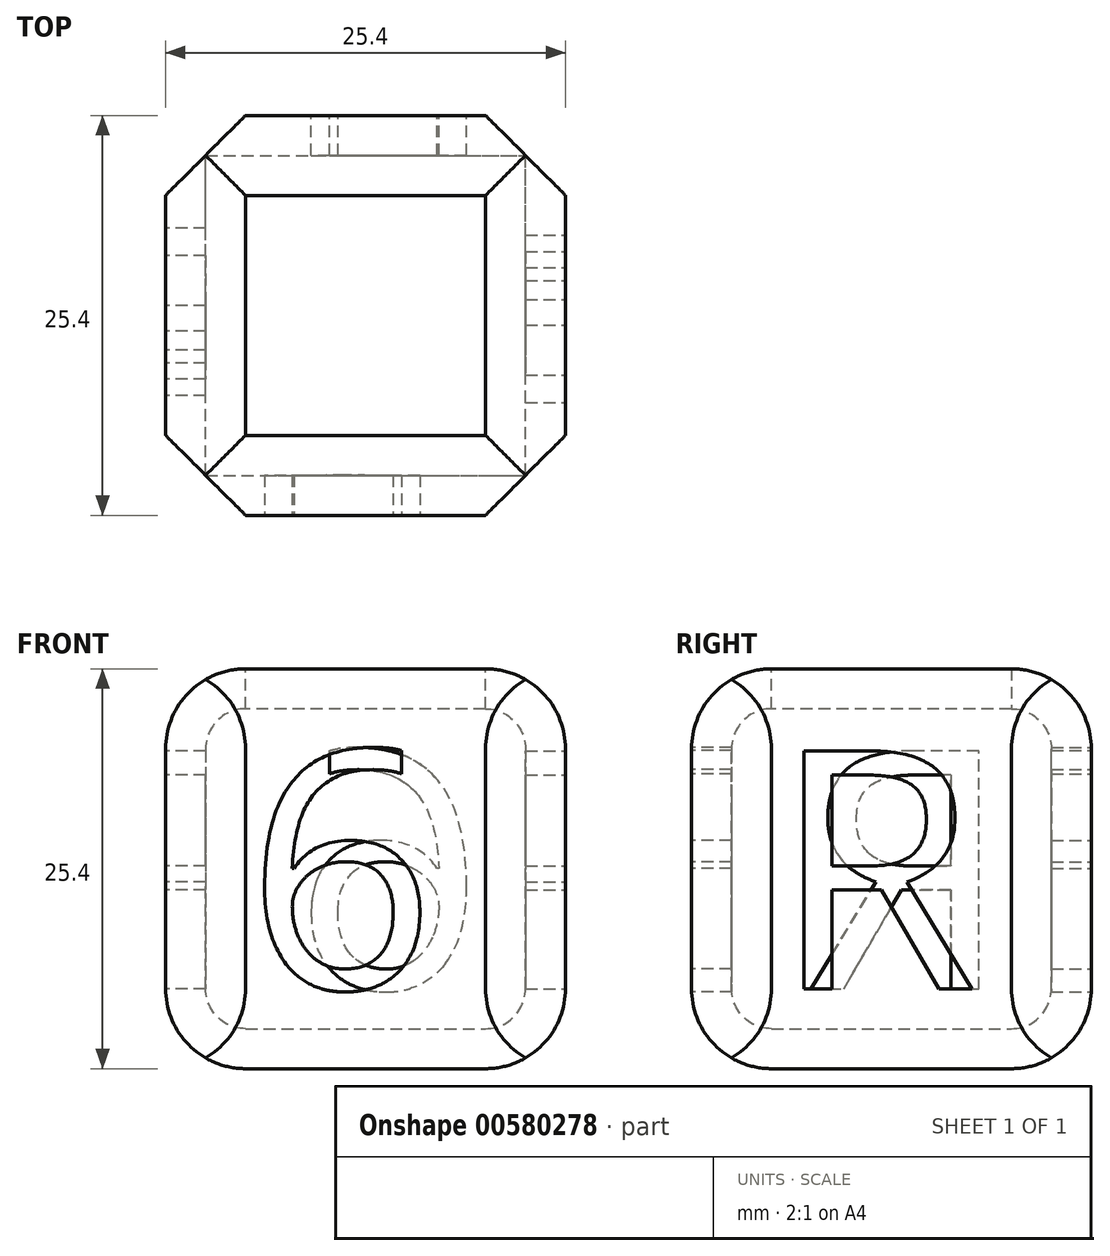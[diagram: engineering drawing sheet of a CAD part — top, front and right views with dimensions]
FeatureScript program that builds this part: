
annotation { "Feature Type Name" : "Feature", "Feature Type Description" : "" }
export const myFeature = defineFeature(function(context is Context, id is Id, definition is map)
    precondition{}
    {
        {
            var Q0;
            Q0=qCreatedBy(makeId("Front.planeOp"),FACE);
            var sketch = newSketch(context, id + "F0", { "sketchPlane" : qUnion([Q0])});
            skLineSegment(sketch, "E0.bottom", {"start": v(-12.7, 12.7) * mm, "end": v(12.7, 12.7) * mm});
            skLineSegment(sketch, "E0.top", {"start": v(-12.7, -12.7) * mm, "end": v(12.7, -12.7) * mm});
            skLineSegment(sketch, "E0.left", {"start": v(-12.7, 12.7) * mm, "end": v(-12.7, -12.7) * mm});
            skLineSegment(sketch, "E0.right", {"start": v(12.7, 12.7) * mm, "end": v(12.7, -12.7) * mm});
            skPoint(sketch, "E0.middle", {"position": v(0, 0) * mm});
            skSolve(sketch);
        }
        {
            var Q0;
            Q0=makeQuery(id+"F0.imprint","IMPRINT",FACE,{"disambiguationData":[TD([[makeQuery(id+"F0.imprint","IMPRINT",EDGE,{"derivedFrom":sQuery(id+"F0.wireOp",EDGE,"E0.bottom")}),-1.0]])]});
            extrude(context, id + "F1", {"entities" : qUnion([Q0]), "depth" : 25.4 * mm, "offsetDistance" : 25.4 * mm});
        }
        {
            var Q0;
            Q0=makeQuery(id+"F1.opExtrude","SWEPT_FACE",FACE,{"disambiguationData":[OSD([sQuery(id+"F0.wireOp",EDGE,"E0.bottom")])]});
            var Q1;
            Q1=makeQuery(id+"F1.opExtrude","SWEPT_FACE",FACE,{"disambiguationData":[OSD([sQuery(id+"F0.wireOp",EDGE,"E0.top")])]});
            fillet(context, id + "F2", {"entities" : qUnion([Q0, Q1]), "radius" : 5.08 * mm, "tangentPropagation" : true, "allowEdgeOverflow" : false});
        }
        {
            var Q0;
            Q0=makeQuery(id+"F1.opExtrude","CAP_FACE",FACE,{"disambiguationData":[OSD([sQuery(id+"F0.wireOp",EDGE,"E0.bottom"),sQuery(id+"F0.wireOp",EDGE,"E0.top"),sQuery(id+"F0.wireOp",EDGE,"E0.left"),sQuery(id+"F0.wireOp",EDGE,"E0.right")])],"isStart":false});
            var Q1;
            Q1=makeQuery(id+"F1.opExtrude","SWEPT_FACE",FACE,{"disambiguationData":[OSD([sQuery(id+"F0.wireOp",EDGE,"E0.right")])]});
            var Q2;
            Q2=makeQuery(id+"F1.opExtrude","CAP_FACE",FACE,{"disambiguationData":[OSD([sQuery(id+"F0.wireOp",EDGE,"E0.bottom"),sQuery(id+"F0.wireOp",EDGE,"E0.top"),sQuery(id+"F0.wireOp",EDGE,"E0.left"),sQuery(id+"F0.wireOp",EDGE,"E0.right")])],"isStart":true});
            var Q3;
            Q3=makeQuery(id+"F1.opExtrude","SWEPT_FACE",FACE,{"disambiguationData":[OSD([sQuery(id+"F0.wireOp",EDGE,"E0.left")])]});
            chamfer(context, id + "F3", {"entities" : qUnion([Q0, Q1, Q2, Q3]), "width" : 5.08 * mm, "tangentPropagation" : true});
        }
        {
            var Q0;
            {var subQ0=sQuery(id+"F0.wireOp",EDGE,"E0.left");Q0=makeQuery(id+"F3.opChamfer","BLEND_FACE",FACE,{"disambiguationData":[OSD([subQ0]),TDD([makeQuery(id+"F1.opExtrude","CAP_EDGE",EDGE,{"disambiguationData":[OSD([subQ0])],"isStart":false})])]});}
            var Q1;
            {var subQ0=sQuery(id+"F0.wireOp",EDGE,"E0.left");Q1=makeQuery(id+"F3.opChamfer","BLEND_FACE",FACE,{"disambiguationData":[OSD([subQ0]),TDD([makeQuery(id+"F1.opExtrude","CAP_EDGE",EDGE,{"disambiguationData":[OSD([subQ0])],"isStart":true})])]});}
            var Q2;
            {var subQ0=sQuery(id+"F0.wireOp",EDGE,"E0.right");Q2=makeQuery(id+"F3.opChamfer","BLEND_FACE",FACE,{"disambiguationData":[OSD([subQ0]),TDD([makeQuery(id+"F1.opExtrude","CAP_EDGE",EDGE,{"disambiguationData":[OSD([subQ0])],"isStart":true})])]});}
            var Q3;
            {var subQ0=sQuery(id+"F0.wireOp",EDGE,"E0.right");Q3=makeQuery(id+"F3.opChamfer","BLEND_FACE",FACE,{"disambiguationData":[OSD([subQ0]),TDD([makeQuery(id+"F1.opExtrude","CAP_EDGE",EDGE,{"disambiguationData":[OSD([subQ0])],"isStart":false})])]});}
            var Q4;
            Q4=makeQuery(id+"F1.opExtrude","SWEPT_FACE",FACE,{"disambiguationData":[OSD([sQuery(id+"F0.wireOp",EDGE,"E0.bottom")])]});
            shell(context, id + "F4", {"entities" : qUnion([Q0, Q1, Q2, Q3, Q4]), "thickness" : 2.54 * mm});
        }
        {
            var Q0;
            Q0=makeQuery(id+"F1.opExtrude","CAP_FACE",FACE,{"disambiguationData":[OSD([sQuery(id+"F0.wireOp",EDGE,"E0.bottom"),sQuery(id+"F0.wireOp",EDGE,"E0.top"),sQuery(id+"F0.wireOp",EDGE,"E0.left"),sQuery(id+"F0.wireOp",EDGE,"E0.right")])],"isStart":false});
            var sketch = newSketch(context, id + "F5", { "sketchPlane" : qUnion([Q0])});
            skText(sketch, "E1", { "text": "6", "fontName": "OpenSans-Regular.ttf"});
            const initialGuessF5  = {"E1": [-0.00762, -0.00762, 1, 0, 0.01524]};
            skSetInitialGuess(sketch, initialGuessF5);
            skSolve(sketch);
        }
        {
            var Q0;
            Q0 = qSketchRegion(id + "F5", true);
            extrude(context, id + "F6", {"entities" : qUnion([Q0]), "operationType" : NewBodyOperationType.REMOVE, "oppositeDirection" : true, "depth" : 12.7 * mm, "offsetDistance" : 25.4 * mm});
        }
        {
            var Q0;
            Q0=makeQuery(id+"F1.opExtrude","SWEPT_FACE",FACE,{"disambiguationData":[OSD([sQuery(id+"F0.wireOp",EDGE,"E0.left")])]});
            var sketch = newSketch(context, id + "F7", { "sketchPlane" : qUnion([Q0])});
            skText(sketch, "E2", { "text": "R", "fontName": "OpenSans-Regular.ttf"});
            const initialGuessF7  = {"E2": [0.00508, -0.00762, 1, 0, 0.01524]};
            skSetInitialGuess(sketch, initialGuessF7);
            skSolve(sketch);
        }
        {
            var Q0;
            Q0 = qSketchRegion(id + "F7", true);
            extrude(context, id + "F8", {"entities" : qUnion([Q0]), "operationType" : NewBodyOperationType.REMOVE, "oppositeDirection" : true, "depth" : 12.7 * mm, "offsetDistance" : 25.4 * mm});
        }
        {
            var Q0;
            Q0=makeQuery(id+"F1.opExtrude","CAP_FACE",FACE,{"disambiguationData":[OSD([sQuery(id+"F0.wireOp",EDGE,"E0.bottom"),sQuery(id+"F0.wireOp",EDGE,"E0.top"),sQuery(id+"F0.wireOp",EDGE,"E0.left"),sQuery(id+"F0.wireOp",EDGE,"E0.right")])],"isStart":true});
            var sketch = newSketch(context, id + "F9", { "sketchPlane" : qUnion([Q0])});
            skText(sketch, "E3", { "text": "6", "fontName": "OpenSans-Regular.ttf"});
            const initialGuessF9  = {"E3": [-0.00762, -0.00762, 1, 0, 0.01524]};
            skSetInitialGuess(sketch, initialGuessF9);
            skSolve(sketch);
        }
        {
            var Q0;
            Q0 = qSketchRegion(id + "F9", true);
            extrude(context, id + "F10", {"entities" : qUnion([Q0]), "operationType" : NewBodyOperationType.REMOVE, "oppositeDirection" : true, "depth" : 12.7 * mm, "offsetDistance" : 25.4 * mm});
        }
        {
            var Q0;
            Q0=makeQuery(id+"F1.opExtrude","SWEPT_FACE",FACE,{"disambiguationData":[OSD([sQuery(id+"F0.wireOp",EDGE,"E0.right")])]});
            var sketch = newSketch(context, id + "F11", { "sketchPlane" : qUnion([Q0])});
            skText(sketch, "E4", { "text": "R", "fontName": "OpenSans-Regular.ttf"});
            const initialGuessF11  = {"E4": [-0.02032, -0.00762, 1, 0, 0.01524]};
            skSetInitialGuess(sketch, initialGuessF11);
            skSolve(sketch);
        }
        {
            var Q0;
            Q0 = qSketchRegion(id + "F11", true);
            extrude(context, id + "F12", {"entities" : qUnion([Q0]), "operationType" : NewBodyOperationType.REMOVE, "oppositeDirection" : true, "depth" : 12.7 * mm, "offsetDistance" : 25.4 * mm});
        }
    });
